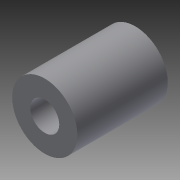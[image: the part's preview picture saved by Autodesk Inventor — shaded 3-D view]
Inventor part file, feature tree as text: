
AUTODESK INVENTOR PART (.ipt)
format: ipt  version: 2015 SP1 (Build 190203100, 203)  size: 87,552 bytes
history: native  units: in
note: dims shown in document units (in); Inventor stores cm internally (conversion verified against a paired STEP export)
features: extrude x3, sketch x3
ambient origin geometry x8: Origin, YZ Plane, XZ Plane, XY Plane, X Axis, Y Axis, Z Axis, Center Point
bodies: Solid1 (feature_tree)
feature tree (6):
  extrude  "Extrusion1"  Depth=0.9843in TaperAngle=0.0deg
  extrude  "Extrusion2"  Depth=0.3937in TaperAngle=0.0deg
  extrude  "Extrusion3"  Depth=0.3937in TaperAngle=0.0deg
  sketch  "Sketch1"  dims[d0=0.7087in d1=0.9843in d2=0.0in]
  sketch  "Sketch2"  dims[d3=0.315in d4=0.3937in d5=0.0in]
  sketch  "Sketch3"  dims[d6=0.1969in d7=0.3937in d8=0.0in]
